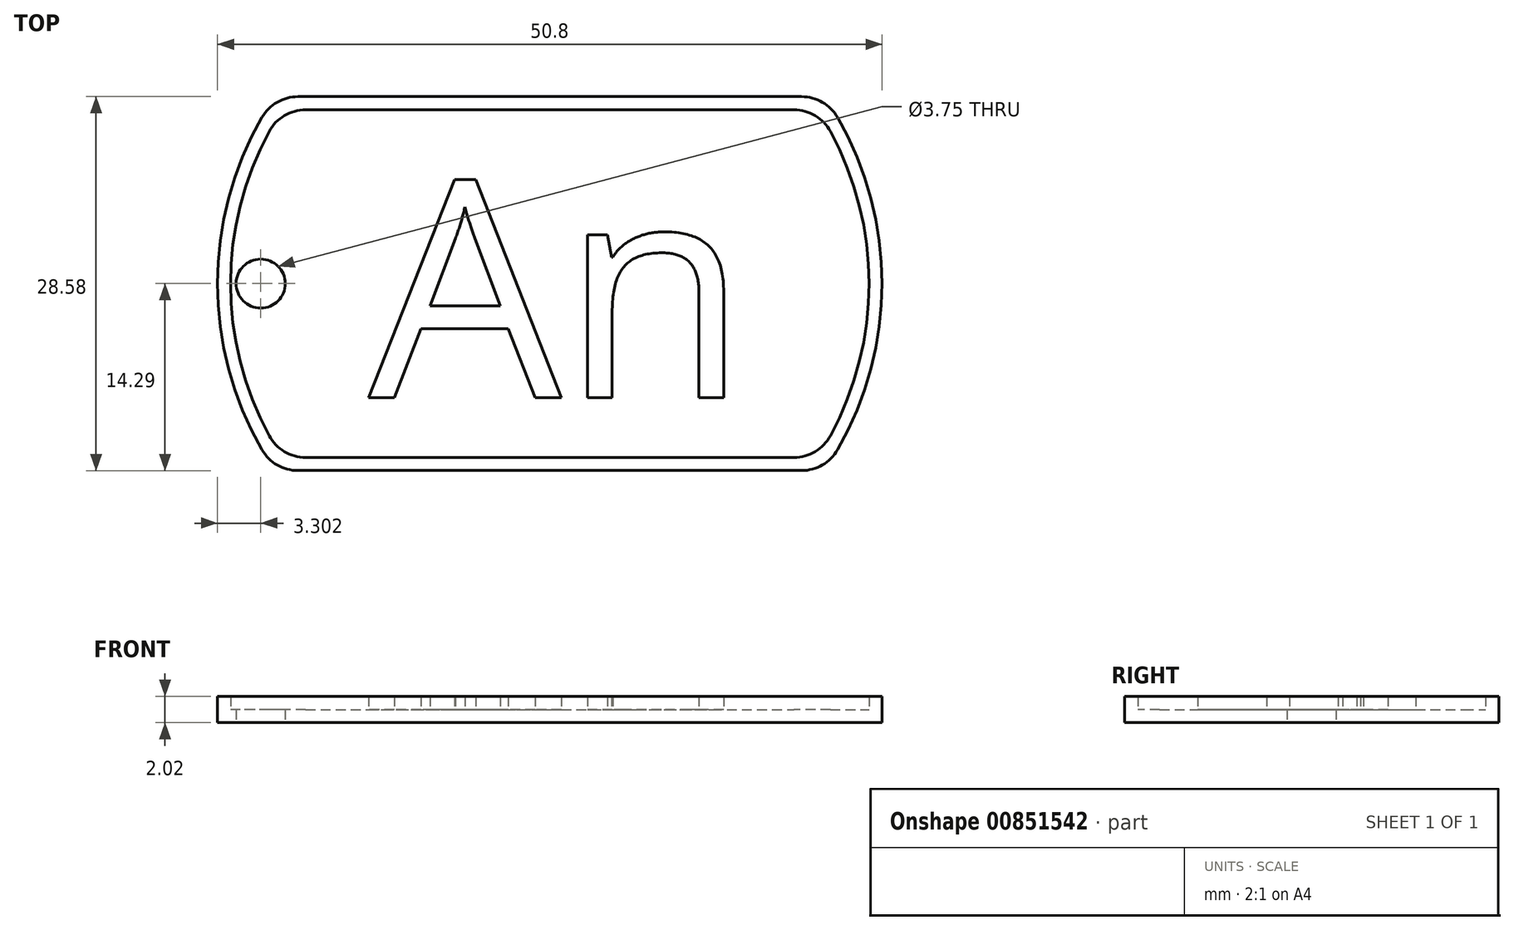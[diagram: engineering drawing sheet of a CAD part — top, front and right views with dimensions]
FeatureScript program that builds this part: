
annotation { "Feature Type Name" : "Feature", "Feature Type Description" : "" }
export const myFeature = defineFeature(function(context is Context, id is Id, definition is map)
    precondition{}
    {
        {
            var Q0;
            Q0=qCreatedBy(makeId("Top.planeOp"),FACE);
            var sketch = newSketch(context, id + "F0", { "sketchPlane" : qUnion([Q0])});
            skArc(sketch, "E0", {"start": v(-22, 12.7) * mm, "mid": v(-25.4, 0) * mm, "end": v(-22, -12.7) * mm});
            skLineSegment(sketch, "E1.top", {"start": v(-19.25, -14.29) * mm, "end": v(19.25, -14.29) * mm});
            skArc(sketch, "E2.trimOffspring", {"start": v(22, -12.7) * mm, "mid": v(25.4, 0) * mm, "end": v(22, 12.7) * mm});
            skLineSegment(sketch, "E3", {"start": v(-19.25, 14.29) * mm, "end": v(19.25, 14.29) * mm});
            skPoint(sketch, "E4.visualSharp", {"position": v(-21, 14.29) * mm});
            skArc(sketch, "E4.filletArc", {"start": v(-19.25, 14.29) * mm, "mid": v(-20.83, 13.86) * mm, "end": v(-22, 12.7) * mm});
            skPoint(sketch, "E5.visualSharp", {"position": v(21, 14.29) * mm});
            skArc(sketch, "E5.filletArc", {"start": v(22, 12.7) * mm, "mid": v(20.83, 13.86) * mm, "end": v(19.25, 14.29) * mm});
            skPoint(sketch, "E6.visualSharp", {"position": v(21, -14.29) * mm});
            skArc(sketch, "E6.filletArc", {"start": v(19.25, -14.29) * mm, "mid": v(20.83, -13.86) * mm, "end": v(22, -12.7) * mm});
            skPoint(sketch, "E7.visualSharp", {"position": v(-21, -14.29) * mm});
            skArc(sketch, "E7.filletArc", {"start": v(-22, -12.7) * mm, "mid": v(-20.83, -13.86) * mm, "end": v(-19.25, -14.29) * mm});
            skCircle(sketch, "E8", {"center": v(-22.1, 0) * mm, "radius": 1.87 * mm});
            skSolve(sketch);
        }
        {
            var Q0;
            Q0=makeQuery(id+"F0.imprint","IMPRINT",FACE,{"disambiguationData":[TD([[makeQuery(id+"F0.imprint","IMPRINT",EDGE,{"derivedFrom":sQuery(id+"F0.wireOp",EDGE,"E0")}),1.0]])]});
            extrude(context, id + "F1", {"entities" : qUnion([Q0]), "depth" : 1 * mm, "offsetDistance" : 25.4 * mm});
        }
        {
            var Q0;
            Q0=makeQuery(id+"F1.opExtrude","CAP_FACE",FACE,{"disambiguationData":[OSD([sQuery(id+"F0.wireOp",EDGE,"E0"),sQuery(id+"F0.wireOp",EDGE,"E1.top"),sQuery(id+"F0.wireOp",EDGE,"E2.trimOffspring"),sQuery(id+"F0.wireOp",EDGE,"E3"),sQuery(id+"F0.wireOp",EDGE,"E4.filletArc"),sQuery(id+"F0.wireOp",EDGE,"E5.filletArc"),sQuery(id+"F0.wireOp",EDGE,"E6.filletArc"),sQuery(id+"F0.wireOp",EDGE,"E7.filletArc")])],"isStart":false});
            var sketch = newSketch(context, id + "F2", { "sketchPlane" : qUnion([Q0])});
            skLineSegment(sketch, "E9.0", {"start": v(-18.66, 13.29) * mm, "end": v(18.66, 13.29) * mm});
            skArc(sketch, "E9.1", {"start": v(-21.45, 11.63) * mm, "mid": v(-24.4, 0) * mm, "end": v(-21.45, -11.63) * mm});
            skLineSegment(sketch, "E9.2", {"start": v(-18.66, -13.29) * mm, "end": v(18.66, -13.29) * mm});
            skArc(sketch, "E9.3", {"start": v(21.45, -11.63) * mm, "mid": v(24.4, 0) * mm, "end": v(21.45, 11.63) * mm});
            skPoint(sketch, "E10.visualSharp", {"position": v(-20.46, 13.29) * mm});
            skArc(sketch, "E10.filletArc", {"start": v(-18.66, 13.29) * mm, "mid": v(-20.29, 12.84) * mm, "end": v(-21.45, 11.63) * mm});
            skPoint(sketch, "E11.visualSharp", {"position": v(20.46, 13.29) * mm});
            skArc(sketch, "E11.filletArc", {"start": v(21.45, 11.63) * mm, "mid": v(20.29, 12.84) * mm, "end": v(18.66, 13.29) * mm});
            skPoint(sketch, "E12.visualSharp", {"position": v(20.46, -13.29) * mm});
            skArc(sketch, "E12.filletArc", {"start": v(18.66, -13.29) * mm, "mid": v(20.29, -12.84) * mm, "end": v(21.45, -11.63) * mm});
            skPoint(sketch, "E13.visualSharp", {"position": v(-20.46, -13.29) * mm});
            skArc(sketch, "E13.filletArc", {"start": v(-21.45, -11.63) * mm, "mid": v(-20.29, -12.84) * mm, "end": v(-18.66, -13.29) * mm});
            skLineSegment(sketch, "E14.0", {"start": v(-19.25, 14.29) * mm, "end": v(19.25, 14.29) * mm});
            skArc(sketch, "E14.1", {"start": v(-22, 12.7) * mm, "mid": v(-25.4, 0) * mm, "end": v(-22, -12.7) * mm});
            skLineSegment(sketch, "E14.2", {"start": v(-19.25, -14.29) * mm, "end": v(19.25, -14.29) * mm});
            skArc(sketch, "E14.3", {"start": v(22, -12.7) * mm, "mid": v(25.4, 0) * mm, "end": v(22, 12.7) * mm});
            skPoint(sketch, "E15.visualSharp", {"position": v(-21, -14.29) * mm});
            skArc(sketch, "E15.filletArc", {"start": v(-22, -12.7) * mm, "mid": v(-20.83, -13.86) * mm, "end": v(-19.25, -14.29) * mm});
            skPoint(sketch, "E16.visualSharp", {"position": v(21, -14.29) * mm});
            skArc(sketch, "E16.filletArc", {"start": v(19.25, -14.29) * mm, "mid": v(20.83, -13.86) * mm, "end": v(22, -12.7) * mm});
            skPoint(sketch, "E17.visualSharp", {"position": v(21, 14.29) * mm});
            skArc(sketch, "E17.filletArc", {"start": v(22, 12.7) * mm, "mid": v(20.83, 13.86) * mm, "end": v(19.25, 14.29) * mm});
            skPoint(sketch, "E18.visualSharp", {"position": v(-21, 14.29) * mm});
            skArc(sketch, "E18.filletArc", {"start": v(-19.25, 14.29) * mm, "mid": v(-20.83, 13.86) * mm, "end": v(-22, 12.7) * mm});
            skSolve(sketch);
        }
        {
            var Q0;
            Q0=makeQuery(id+"F2.imprint","IMPRINT",FACE,{"disambiguationData":[TD([[makeQuery(id+"F2.imprint","IMPRINT",EDGE,{"derivedFrom":sQuery(id+"F2.wireOp",EDGE,"E9.0")}),1.0]])]});
            extrude(context, id + "F3", {"entities" : qUnion([Q0]), "operationType" : NewBodyOperationType.ADD, "depth" : 1 * mm, "offsetDistance" : 25.4 * mm});
        }
        {
            var Q0;
            Q0=makeQuery(id+"F1.opExtrude","CAP_FACE",FACE,{"disambiguationData":[OSD([sQuery(id+"F0.wireOp",EDGE,"E0"),sQuery(id+"F0.wireOp",EDGE,"E1.top"),sQuery(id+"F0.wireOp",EDGE,"E2.trimOffspring"),sQuery(id+"F0.wireOp",EDGE,"E3"),sQuery(id+"F0.wireOp",EDGE,"E4.filletArc"),sQuery(id+"F0.wireOp",EDGE,"E5.filletArc"),sQuery(id+"F0.wireOp",EDGE,"E6.filletArc"),sQuery(id+"F0.wireOp",EDGE,"E7.filletArc"),sQuery(id+"F0.wireOp",EDGE,"E8")])],"isStart":false});
            var sketch = newSketch(context, id + "F4", { "sketchPlane" : qUnion([Q0])});
            skText(sketch, "E19", { "text": "An", "fontName": "OpenSans-Regular.ttf"});
            const initialGuessF4  = {"E19": [-0.01384, -0.00872, 1, 0, 0.01675]};
            skSetInitialGuess(sketch, initialGuessF4);
            skSolve(sketch);
        }
        {
            var Q0;
            Q0 = qSketchRegion(id + "F4", true);
            extrude(context, id + "F5", {"entities" : qUnion([Q0]), "operationType" : NewBodyOperationType.ADD, "depth" : 1.02 * mm, "offsetDistance" : 25.4 * mm});
        }
    });
